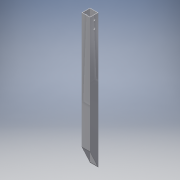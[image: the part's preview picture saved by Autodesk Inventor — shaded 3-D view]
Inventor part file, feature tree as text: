
AUTODESK INVENTOR PART (.ipt)
format: ipt  version: 2016 (Build 200138000, 138)  size: 126,976 bytes
history: native  units: in
note: dims shown in document units (in); Inventor stores cm internally (conversion verified against a paired STEP export)
features: sketch x4, other x3
ambient origin geometry x8: Origin, YZ Plane, XZ Plane, XY Plane, X Axis, Y Axis, Z Axis, Center Point
bodies: Solid1 (feature_tree)
feature tree (7):
  other  "top.ipt"
  other  "Solid1::top.ipt"
  other  "TaggingFeature1"
  sketch  "Sketch1"  dims[d0=0.3937in]
  sketch  "Sketch2"
  sketch  "Sketch3"
  sketch  "Sketch4"
